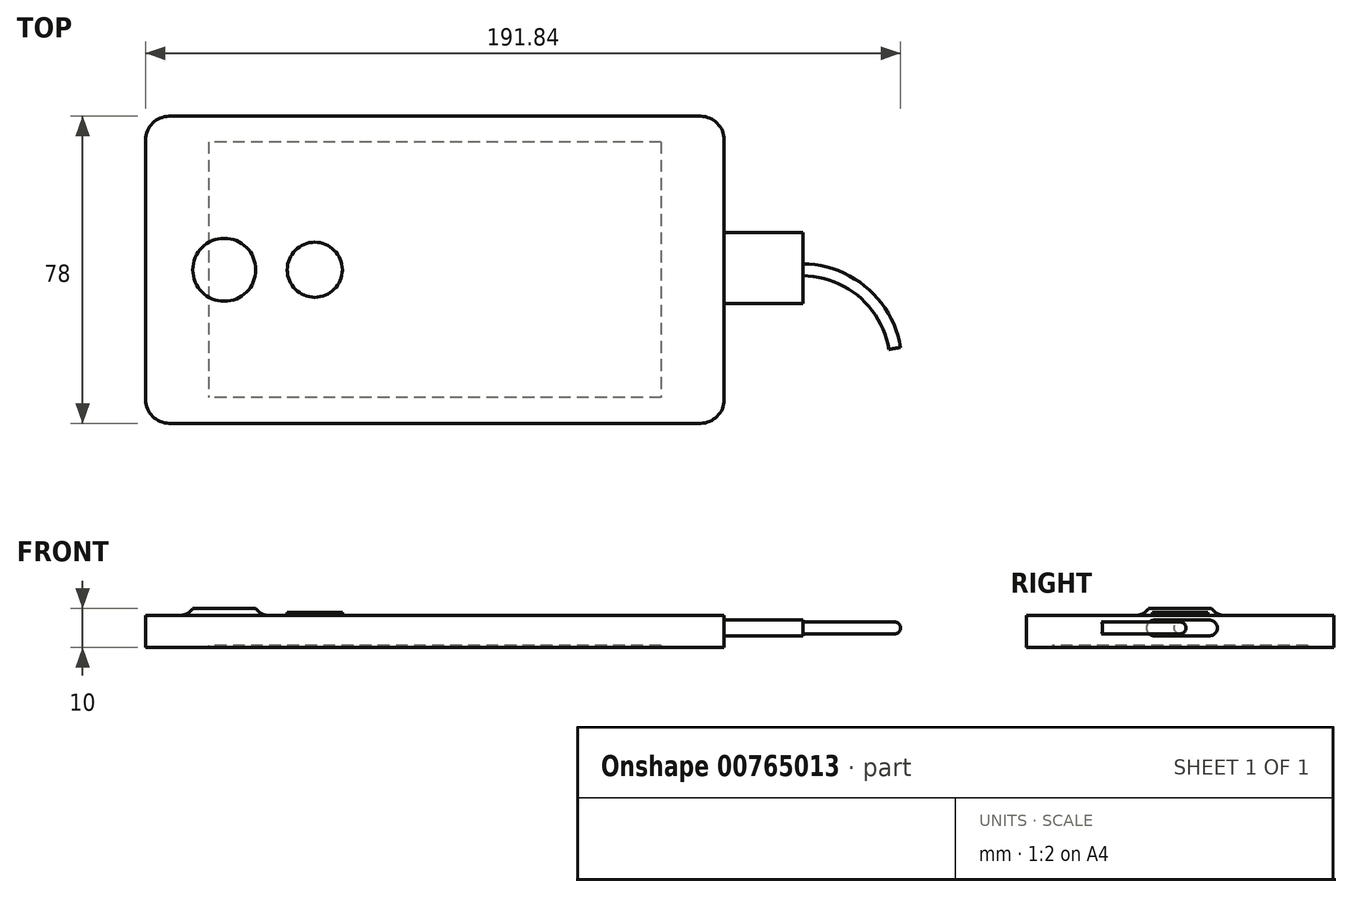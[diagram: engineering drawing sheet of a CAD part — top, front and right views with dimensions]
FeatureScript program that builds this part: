
annotation { "Feature Type Name" : "Feature", "Feature Type Description" : "" }
export const myFeature = defineFeature(function(context is Context, id is Id, definition is map)
    precondition{}
    {
        {
            var Q0;
            Q0=qCreatedBy(makeId("Top.planeOp"),FACE);
            var sketch = newSketch(context, id + "F0", { "sketchPlane" : qUnion([Q0])});
            skLineSegment(sketch, "E0.bottom", {"start": v(67.5, -39) * mm, "end": v(-67.5, -39) * mm});
            skLineSegment(sketch, "E0.top", {"start": v(67.5, 39) * mm, "end": v(-67.5, 39) * mm});
            skLineSegment(sketch, "E0.left", {"start": v(73.5, -33) * mm, "end": v(73.5, 33) * mm});
            skLineSegment(sketch, "E0.right", {"start": v(-73.5, -33) * mm, "end": v(-73.5, 33) * mm});
            skPoint(sketch, "E0.middle", {"position": v(0, 0) * mm});
            skPoint(sketch, "E1.visualSharp", {"position": v(-73.5, 39) * mm});
            skArc(sketch, "E1.filletArc", {"start": v(-67.5, 39) * mm, "mid": v(-71.74, 37.24) * mm, "end": v(-73.5, 33) * mm});
            skPoint(sketch, "E2.visualSharp", {"position": v(73.5, 39) * mm});
            skArc(sketch, "E2.filletArc", {"start": v(73.5, 33) * mm, "mid": v(71.74, 37.24) * mm, "end": v(67.5, 39) * mm});
            skPoint(sketch, "E3.visualSharp", {"position": v(73.5, -39) * mm});
            skArc(sketch, "E3.filletArc", {"start": v(67.5, -39) * mm, "mid": v(71.74, -37.24) * mm, "end": v(73.5, -33) * mm});
            skPoint(sketch, "E4.visualSharp", {"position": v(-73.5, -39) * mm});
            skArc(sketch, "E4.filletArc", {"start": v(-73.5, -33) * mm, "mid": v(-71.74, -37.24) * mm, "end": v(-67.5, -39) * mm});
            skCircle(sketch, "E5", {"center": v(-53.5, 0) * mm, "radius": 8 * mm});
            skCircle(sketch, "E6", {"center": v(-30.5, 0) * mm, "radius": 7 * mm});
            skSolve(sketch);
        }
        {
            var Q0;
            Q0=makeQuery(id+"F0.imprint","IMPRINT",FACE,{"disambiguationData":[TD([[makeQuery(id+"F0.imprint","IMPRINT",EDGE,{"derivedFrom":sQuery(id+"F0.wireOp",EDGE,"E5")}),1.0]])]});
            var Q1;
            Q1=makeQuery(id+"F0.imprint","IMPRINT",FACE,{"disambiguationData":[TD([[makeQuery(id+"F0.imprint","IMPRINT",EDGE,{"derivedFrom":sQuery(id+"F0.wireOp",EDGE,"E0.bottom")}),-1.0]])]});
            var Q2;
            Q2=makeQuery(id+"F0.imprint","IMPRINT",FACE,{"disambiguationData":[TD([[makeQuery(id+"F0.imprint","IMPRINT",EDGE,{"derivedFrom":sQuery(id+"F0.wireOp",EDGE,"E6")}),1.0]])]});
            extrude(context, id + "F1", {"entities" : qUnion([Q0, Q1, Q2]), "depth" : 8.15 * mm, "offsetDistance" : 25 * mm});
        }
        {
            var Q0;
            Q0=makeQuery(id+"F0.imprint","IMPRINT",FACE,{"disambiguationData":[TD([[makeQuery(id+"F0.imprint","IMPRINT",EDGE,{"derivedFrom":sQuery(id+"F0.wireOp",EDGE,"E5")}),1.0]])]});
            extrude(context, id + "F2", {"entities" : qUnion([Q0]), "operationType" : NewBodyOperationType.ADD, "depth" : 10 * mm, "offsetDistance" : 25 * mm});
        }
        {
            var Q0;
            Q0=makeQuery(id+"F0.imprint","IMPRINT",FACE,{"disambiguationData":[TD([[makeQuery(id+"F0.imprint","IMPRINT",EDGE,{"derivedFrom":sQuery(id+"F0.wireOp",EDGE,"E6")}),1.0]])]});
            extrude(context, id + "F3", {"entities" : qUnion([Q0]), "operationType" : NewBodyOperationType.ADD, "depth" : 9 * mm, "offsetDistance" : 25 * mm});
        }
        {
            var Q0;
            Q0=makeQuery(id+"F2.boolean.opBoolean","INTERSECT",EDGE,{"derivedFrom":[makeQuery(id+"F1.opExtrude","CAP_FACE",FACE,{"disambiguationData":[OSD([sQuery(id+"F0.wireOp",EDGE,"E0.bottom"),sQuery(id+"F0.wireOp",EDGE,"E0.top"),sQuery(id+"F0.wireOp",EDGE,"E0.left"),sQuery(id+"F0.wireOp",EDGE,"E0.right"),sQuery(id+"F0.wireOp",EDGE,"E1.filletArc"),sQuery(id+"F0.wireOp",EDGE,"E2.filletArc"),sQuery(id+"F0.wireOp",EDGE,"E3.filletArc"),sQuery(id+"F0.wireOp",EDGE,"E4.filletArc")])],"isStart":false}),makeQuery(id+"F2.opExtrude","SWEPT_FACE",FACE,{"disambiguationData":[OSD([sQuery(id+"F0.wireOp",EDGE,"E5")])]})]});
            fillet(context, id + "F4", {"entities" : qUnion([Q0]), "radius" : 4 * mm, "tangentPropagation" : true, "allowEdgeOverflow" : false});
        }
        {
            var Q0;
            Q0=qCreatedBy(makeId("Top.planeOp"),FACE);
            var sketch = newSketch(context, id + "F5", { "sketchPlane" : qUnion([Q0])});
            skLineSegment(sketch, "E7.bottom", {"start": v(57.5, 32.5) * mm, "end": v(-57.5, 32.5) * mm});
            skLineSegment(sketch, "E7.top", {"start": v(57.5, -32.5) * mm, "end": v(-57.5, -32.5) * mm});
            skLineSegment(sketch, "E7.left", {"start": v(57.5, 32.5) * mm, "end": v(57.5, -32.5) * mm});
            skLineSegment(sketch, "E7.right", {"start": v(-57.5, 32.5) * mm, "end": v(-57.5, -32.5) * mm});
            skPoint(sketch, "E7.middle", {"position": v(0, 0) * mm});
            skSolve(sketch);
        }
        {
            var Q0;
            Q0=makeQuery(id+"F5.imprint","IMPRINT",FACE,{"disambiguationData":[TD([[makeQuery(id+"F5.imprint","IMPRINT",EDGE,{"derivedFrom":sQuery(id+"F5.wireOp",EDGE,"E7.bottom")}),1.0]])]});
            extrude(context, id + "F6", {"entities" : qUnion([Q0]), "operationType" : NewBodyOperationType.REMOVE, "depth" : 0.5 * mm, "offsetDistance" : 25 * mm});
        }
        {
            var Q0;
            Q0=makeQuery(id+"F1.opExtrude","SWEPT_FACE",FACE,{"disambiguationData":[OSD([sQuery(id+"F0.wireOp",EDGE,"E0.left")])]});
            var sketch = newSketch(context, id + "F7", { "sketchPlane" : qUnion([Q0])});
            skLineSegment(sketch, "E8", {"start": v(7.45, 5) * mm, "end": v(-6.55, 5) * mm});
            skArc(sketch, "E9.0.startCap", {"start": v(7.45, 7) * mm, "mid": v(9.45, 5) * mm, "end": v(7.45, 3) * mm});
            skArc(sketch, "E9.0.endCap", {"start": v(-6.55, 3) * mm, "mid": v(-8.55, 5) * mm, "end": v(-6.55, 7) * mm});
            skLineSegment(sketch, "E9.0.left", {"start": v(7.45, 3) * mm, "end": v(-6.55, 3) * mm});
            skLineSegment(sketch, "E9.0.right", {"start": v(7.45, 7) * mm, "end": v(-6.55, 7) * mm});
            skCircle(sketch, "E10", {"center": v(0, 5) * mm, "radius": 1.5 * mm});
            skSolve(sketch);
        }
        {
            var Q0;
            Q0=qSketchRegion(id+"F7",true);
            var Q1;
            {var subQ0=sQuery(id+"F7.wireOp",EDGE,"E10");var subQ1=sQuery(id+"F7.wireOp",EDGE,"E8");var subQ2=makeQuery(id+"F7.imprint","INTERSECT",VERTEX,{"disambiguationData":[OD(0.0)],"derivedFrom":[subQ1,subQ0]});Q1=makeQuery(id+"F7.imprint","IMPRINT",FACE,{"disambiguationData":[TD([[makeQuery(id+"F7.imprint","IMPRINT",EDGE,{"disambiguationData":[TD([[subQ2,1.0]])],"derivedFrom":subQ1}),-1.0]])]});}
            var Q2;
            {var subQ0=sQuery(id+"F7.wireOp",EDGE,"E10");var subQ1=sQuery(id+"F7.wireOp",EDGE,"E8");var subQ2=makeQuery(id+"F7.imprint","INTERSECT",VERTEX,{"disambiguationData":[OD(0.0)],"derivedFrom":[subQ1,subQ0]});Q2=makeQuery(id+"F7.imprint","IMPRINT",FACE,{"disambiguationData":[TD([[makeQuery(id+"F7.imprint","IMPRINT",EDGE,{"disambiguationData":[TD([[subQ2,1.0]])],"derivedFrom":subQ1}),1.0]])]});}
            extrude(context, id + "F8", {"entities" : qUnion([Q0, Q1, Q2]), "operationType" : NewBodyOperationType.ADD, "depth" : 20 * mm, "offsetDistance" : 25 * mm});
        }
        {
            var Q0;
            Q0=makeQuery(id+"F8.opExtrude","SWEPT_FACE",FACE,{"disambiguationData":[OSD([sQuery(id+"F7.wireOp",EDGE,"E9.0.left")])]});
            cPlane(context, id + "F9", {"entities" : qUnion([Q0]), "cplaneType" : CPlaneType.OFFSET, "offset" : 2 * mm, "oppositeDirection" : true, "width" : 150 * mm, "height" : 150 * mm});
        }
        {
            var Q0;
            Q0=qCreatedBy(id+"F9.planeOp",FACE);
            var sketch = newSketch(context, id + "F10", { "sketchPlane" : qUnion([Q0])});
            skArc(sketch, "E11", {"start": v(93.5, 0) * mm, "mid": v(108.81, 5.74) * mm, "end": v(116.86, 19.97) * mm});
            skLineSegment(sketch, "E12.0", {"start": v(93.5, -7.45) * mm, "end": v(93.5, 6.55) * mm});
            skSolve(sketch);
        }
        {
            var Q0;
            Q0=makeQuery(id+"F8.opExtrude","CAP_FACE",FACE,{"disambiguationData":[OSD([sQuery(id+"F7.wireOp",EDGE,"E8"),sQuery(id+"F7.wireOp",EDGE,"E9.0.startCap"),sQuery(id+"F7.wireOp",EDGE,"E9.0.endCap"),sQuery(id+"F7.wireOp",EDGE,"E9.0.left"),sQuery(id+"F7.wireOp",EDGE,"E9.0.right"),sQuery(id+"F7.wireOp",EDGE,"E10")])],"isStart":false});
            var sketch = newSketch(context, id + "F11", { "sketchPlane" : qUnion([Q0])});
            skCircle(sketch, "E13.0", {"center": v(0, 5) * mm, "radius": 1.5 * mm});
            skSolve(sketch);
        }
        {
            var Q0;
            Q0=makeQuery(id+"F11.imprint","IMPRINT",FACE,{"disambiguationData":[TD([[makeQuery(id+"F11.imprint","IMPRINT",EDGE,{"derivedFrom":sQuery(id+"F11.wireOp",EDGE,"E13.0")}),1.0]])]});
            var Q1;
            Q1=sQuery(id+"F10.wireOp",EDGE,"E11");
            sweep(context, id + "F12", {"operationType" : NewBodyOperationType.ADD, "profiles" : qUnion([Q0]), "path" : qUnion([Q1])});
        }
    });
